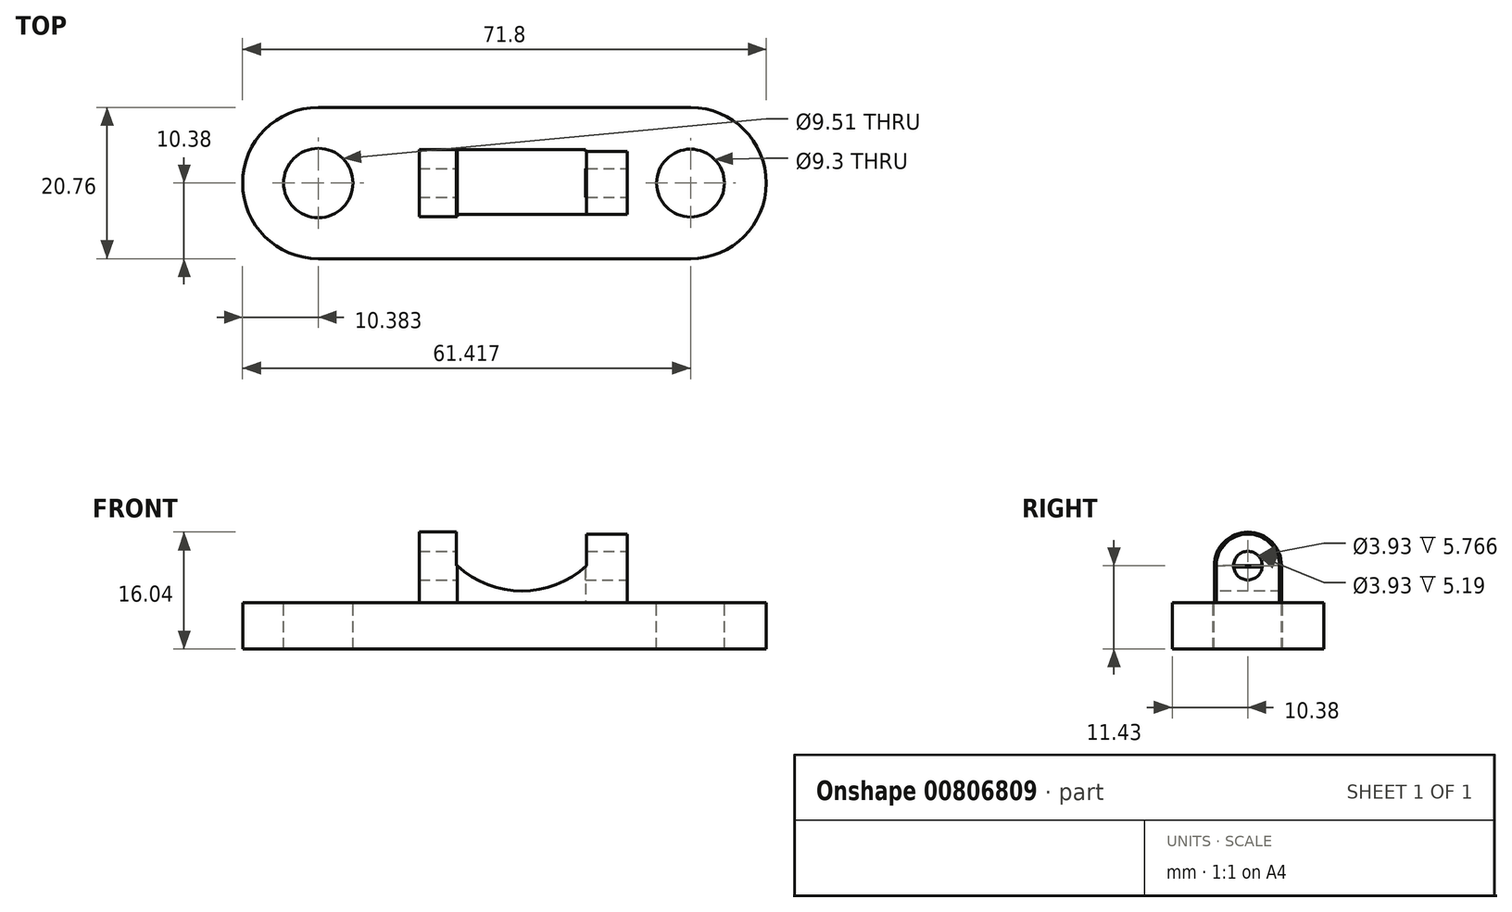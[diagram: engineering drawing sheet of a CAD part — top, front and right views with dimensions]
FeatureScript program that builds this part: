
annotation { "Feature Type Name" : "Feature", "Feature Type Description" : "" }
export const myFeature = defineFeature(function(context is Context, id is Id, definition is map)
    precondition{}
    {
        {
            var Q0;
            Q0=qCreatedBy(makeId("Top.planeOp"),FACE);
            var sketch = newSketch(context, id + "F0", { "sketchPlane" : qUnion([Q0])});
            skLineSegment(sketch, "E0.bottom", {"start": v(25.52, -10.38) * mm, "end": v(-25.52, -10.38) * mm});
            skLineSegment(sketch, "E0.top", {"start": v(25.52, 10.38) * mm, "end": v(-25.52, 10.38) * mm});
            skLineSegment(sketch, "E0.left", {"start": v(25.52, -10.38) * mm, "end": v(25.52, 10.38) * mm});
            skLineSegment(sketch, "E0.right", {"start": v(-25.52, -10.38) * mm, "end": v(-25.52, 10.38) * mm});
            skPoint(sketch, "E0.middle", {"position": v(0, 0) * mm});
            skArc(sketch, "E1", {"start": v(-25.52, 10.38) * mm, "mid": v(-35.9, 0) * mm, "end": v(-25.52, -10.38) * mm});
            skArc(sketch, "E2", {"start": v(25.52, -10.38) * mm, "mid": v(35.9, 0) * mm, "end": v(25.52, 10.38) * mm});
            skSolve(sketch);
        }
        {
            var Q0;
            Q0=makeQuery(id+"F0.imprint","IMPRINT",FACE,{"disambiguationData":[TD([[makeQuery(id+"F0.imprint","IMPRINT",EDGE,{"derivedFrom":sQuery(id+"F0.wireOp",EDGE,"E0.right")}),1.0]])]});
            var Q1;
            Q1=makeQuery(id+"F0.imprint","IMPRINT",FACE,{"disambiguationData":[TD([[makeQuery(id+"F0.imprint","IMPRINT",EDGE,{"derivedFrom":sQuery(id+"F0.wireOp",EDGE,"E0.bottom")}),-1.0]])]});
            var Q2;
            Q2=makeQuery(id+"F0.imprint","IMPRINT",FACE,{"disambiguationData":[TD([[makeQuery(id+"F0.imprint","IMPRINT",EDGE,{"derivedFrom":sQuery(id+"F0.wireOp",EDGE,"E0.left")}),-1.0]])]});
            extrude(context, id + "F1", {"entities" : qUnion([Q0, Q1, Q2]), "depth" : 25.4 * mm, "offsetDistance" : 25.4 * mm});
        }
        {
            var Q0;
            Q0=makeQuery(id+"F1.opExtrude","CAP_FACE",FACE,{"disambiguationData":[OSD([sQuery(id+"F0.wireOp",EDGE,"E0.bottom"),sQuery(id+"F0.wireOp",EDGE,"E0.top"),sQuery(id+"F0.wireOp",EDGE,"E1"),sQuery(id+"F0.wireOp",EDGE,"E2")])],"isStart":false});
            var sketch = newSketch(context, id + "F2", { "sketchPlane" : qUnion([Q0])});
            skCircle(sketch, "E3", {"center": v(-25.52, 0) * mm, "radius": 4.76 * mm});
            skCircle(sketch, "E4", {"center": v(25.52, 0) * mm, "radius": 4.65 * mm});
            skSolve(sketch);
        }
        {
            var Q0;
            Q0=makeQuery(id+"F2.imprint","IMPRINT",FACE,{"disambiguationData":[TD([[makeQuery(id+"F2.imprint","IMPRINT",EDGE,{"derivedFrom":sQuery(id+"F2.wireOp",EDGE,"E4")}),1.0]])]});
            var Q1;
            Q1=makeQuery(id+"F2.imprint","IMPRINT",FACE,{"disambiguationData":[TD([[makeQuery(id+"F2.imprint","IMPRINT",EDGE,{"derivedFrom":sQuery(id+"F2.wireOp",EDGE,"E3")}),1.0]])]});
            extrude(context, id + "F3", {"entities" : qUnion([Q0, Q1]), "operationType" : NewBodyOperationType.REMOVE, "oppositeDirection" : true, "depth" : 50.8 * mm, "offsetDistance" : 25.4 * mm});
        }
        {
            var Q0;
            Q0=makeQuery(id+"F1.opExtrude","CAP_FACE",FACE,{"disambiguationData":[OSD([sQuery(id+"F0.wireOp",EDGE,"E0.bottom"),sQuery(id+"F0.wireOp",EDGE,"E0.top"),sQuery(id+"F0.wireOp",EDGE,"E1"),sQuery(id+"F0.wireOp",EDGE,"E2")])],"isStart":false});
            extrude(context, id + "F4", {"entities" : qUnion([Q0]), "operationType" : NewBodyOperationType.REMOVE, "oppositeDirection" : true, "depth" : 19.05 * mm, "offsetDistance" : 25.4 * mm});
        }
        {
            var Q0;
            Q0=makeQuery(id+"F4.boolean.opBoolean","COPY",FACE,{"derivedFrom":makeQuery(id+"F4.opExtrude","CAP_FACE",FACE,{"disambiguationData":[OSD([sQuery(id+"F0.wireOp",EDGE,"E0.bottom"),sQuery(id+"F0.wireOp",EDGE,"E0.top"),sQuery(id+"F0.wireOp",EDGE,"E1"),sQuery(id+"F0.wireOp",EDGE,"E2")])],"isStart":false})});
            var sketch = newSketch(context, id + "F5", { "sketchPlane" : qUnion([Q0])});
            skLineSegment(sketch, "E5.bottom", {"start": v(-6.49, -4.61) * mm, "end": v(-11.68, -4.61) * mm});
            skLineSegment(sketch, "E5.top", {"start": v(-6.49, 4.61) * mm, "end": v(-11.68, 4.61) * mm});
            skLineSegment(sketch, "E5.left", {"start": v(-6.49, -4.61) * mm, "end": v(-6.49, 4.61) * mm});
            skLineSegment(sketch, "E5.right", {"start": v(-11.68, -4.61) * mm, "end": v(-11.68, 4.61) * mm});
            skPoint(sketch, "E5.middle", {"position": v(-9.08, 0) * mm});
            skLineSegment(sketch, "E6.bottom", {"start": v(16.87, -4.32) * mm, "end": v(11.1, -4.32) * mm});
            skLineSegment(sketch, "E6.top", {"start": v(16.87, 4.32) * mm, "end": v(11.1, 4.32) * mm});
            skLineSegment(sketch, "E6.left", {"start": v(16.87, -4.32) * mm, "end": v(16.87, 4.32) * mm});
            skLineSegment(sketch, "E6.right", {"start": v(11.1, -4.32) * mm, "end": v(11.1, 4.32) * mm});
            skPoint(sketch, "E6.middle", {"position": v(13.98, 0) * mm});
            skSolve(sketch);
        }
        {
            var Q0;
            Q0=makeQuery(id+"F5.imprint","IMPRINT",FACE,{"disambiguationData":[TD([[makeQuery(id+"F5.imprint","IMPRINT",EDGE,{"derivedFrom":sQuery(id+"F5.wireOp",EDGE,"E5.bottom")}),-1.0]])]});
            var Q1;
            Q1=makeQuery(id+"F5.imprint","IMPRINT",FACE,{"disambiguationData":[TD([[makeQuery(id+"F5.imprint","IMPRINT",EDGE,{"derivedFrom":sQuery(id+"F5.wireOp",EDGE,"E6.bottom")}),-1.0]])]});
            extrude(context, id + "F6", {"entities" : qUnion([Q0, Q1]), "operationType" : NewBodyOperationType.ADD, "depth" : 5.08 * mm, "offsetDistance" : 25.4 * mm});
        }
        {
            var Q0;
            Q0=makeQuery(id+"F6.opExtrude","SWEPT_FACE",FACE,{"disambiguationData":[OSD([sQuery(id+"F5.wireOp",EDGE,"E5.right")])]});
            var sketch = newSketch(context, id + "F7", { "sketchPlane" : qUnion([Q0])});
            skArc(sketch, "E7", {"start": v(4.61, 11.43) * mm, "mid": v(0, 16.04) * mm, "end": v(-4.61, 11.43) * mm});
            skSolve(sketch);
        }
        {
            var Q0;
            Q0=makeQuery(id+"F7.imprint","IMPRINT",FACE,{"disambiguationData":[TD([[makeQuery(id+"F7.imprint","IMPRINT",EDGE,{"derivedFrom":sQuery(id+"F7.wireOp",EDGE,"E7")}),1.0]])]});
            extrude(context, id + "F8", {"entities" : qUnion([Q0]), "operationType" : NewBodyOperationType.ADD, "depth" : -5.08 * mm, "offsetDistance" : 25.4 * mm});
        }
        {
            var Q0;
            Q0=makeQuery(id+"F6.opExtrude","SWEPT_FACE",FACE,{"disambiguationData":[OSD([sQuery(id+"F5.wireOp",EDGE,"E6.left")])]});
            var sketch = newSketch(context, id + "F9", { "sketchPlane" : qUnion([Q0])});
            skArc(sketch, "E8", {"start": v(4.32, 11.43) * mm, "mid": v(0, 15.75) * mm, "end": v(-4.32, 11.43) * mm});
            skSolve(sketch);
        }
        {
            var Q0;
            Q0=makeQuery(id+"F9.imprint","IMPRINT",FACE,{"disambiguationData":[TD([[makeQuery(id+"F9.imprint","IMPRINT",EDGE,{"derivedFrom":sQuery(id+"F9.wireOp",EDGE,"E8")}),1.0]])]});
            extrude(context, id + "F10", {"entities" : qUnion([Q0]), "operationType" : NewBodyOperationType.ADD, "depth" : -5.6 * mm, "offsetDistance" : 25.4 * mm});
        }
        {
            var Q0;
            {var subQ0=sQuery(id+"F5.wireOp",EDGE,"E6.left");Q0=makeQuery(id+"F10.boolean.opBoolean","MERGE",FACE,{"derivedFrom":[makeQuery(id+"F6.opExtrude","SWEPT_FACE",FACE,{"disambiguationData":[OSD([subQ0])]}),makeQuery(id+"F10.opExtrude","CAP_FACE",FACE,{"disambiguationData":[OSD([subQ0,sQuery(id+"F9.wireOp",EDGE,"E8")])],"isStart":true})]});}
            var sketch = newSketch(context, id + "F11", { "sketchPlane" : qUnion([Q0])});
            skCircle(sketch, "E9", {"center": v(0, 11.43) * mm, "radius": 1.96 * mm});
            skCircle(sketch, "E10", {"center": v(0, 11.43) * mm, "radius": 2.02 * mm});
            skSolve(sketch);
        }
        {
            var Q0;
            Q0=makeQuery(id+"F11.imprint","IMPRINT",FACE,{"disambiguationData":[TD([[makeQuery(id+"F11.imprint","IMPRINT",EDGE,{"derivedFrom":sQuery(id+"F11.wireOp",EDGE,"E9")}),1.0]])]});
            extrude(context, id + "F12", {"entities" : qUnion([Q0]), "operationType" : NewBodyOperationType.REMOVE, "oppositeDirection" : true, "depth" : 50.8 * mm, "offsetDistance" : 25.4 * mm});
        }
        {
            var Q0;
            Q0=makeQuery(id+"F4.boolean.opBoolean","COPY",FACE,{"derivedFrom":makeQuery(id+"F4.opExtrude","CAP_FACE",FACE,{"disambiguationData":[OSD([sQuery(id+"F0.wireOp",EDGE,"E0.bottom"),sQuery(id+"F0.wireOp",EDGE,"E0.top"),sQuery(id+"F0.wireOp",EDGE,"E1"),sQuery(id+"F0.wireOp",EDGE,"E2")])],"isStart":false})});
            var sketch = newSketch(context, id + "F13", { "sketchPlane" : qUnion([Q0])});
            skLineSegment(sketch, "E11.bottom", {"start": v(-6.49, 4.61) * mm, "end": v(11.1, 4.61) * mm});
            skLineSegment(sketch, "E11.top", {"start": v(-6.49, -4.32) * mm, "end": v(11.1, -4.32) * mm});
            skLineSegment(sketch, "E11.left", {"start": v(-6.49, 4.61) * mm, "end": v(-6.49, -4.32) * mm});
            skLineSegment(sketch, "E11.right", {"start": v(11.1, 4.61) * mm, "end": v(11.1, -4.32) * mm});
            skSolve(sketch);
        }
        {
            var Q0;
            {var subQ2=sQuery(id+"F13.wireOp",EDGE,"E11.bottom");Q0=makeQuery(id+"F13.imprint","IMPRINT",FACE,{"disambiguationData":[TD([[makeQuery(id+"F13.imprint","IMPRINT",EDGE,{"derivedFrom":subQ2}),-1.0]])]});}
            extrude(context, id + "F14", {"entities" : qUnion([Q0]), "operationType" : NewBodyOperationType.ADD, "depth" : 5.08 * mm, "offsetDistance" : 25.4 * mm});
        }
        {
            var Q0;
            Q0=makeQuery(id+"F14.boolean.opBoolean","MERGE",FACE,{"derivedFrom":[makeQuery(id+"F6.opExtrude","SWEPT_FACE",FACE,{"disambiguationData":[OSD([sQuery(id+"F5.wireOp",EDGE,"E6.bottom")])]}),makeQuery(id+"F14.opExtrude","SWEPT_FACE",FACE,{"disambiguationData":[OSD([sQuery(id+"F13.wireOp",EDGE,"E11.top")])]})]});
            var sketch = newSketch(context, id + "F15", { "sketchPlane" : qUnion([Q0])});
            skArc(sketch, "E12", {"start": v(-6.49, 11.43) * mm, "mid": v(2.4, 7.96) * mm, "end": v(11.28, 11.43) * mm});
            skSolve(sketch);
        }
        {
            var Q0;
            Q0=makeQuery(id+"F15.imprint","IMPRINT",FACE,{"disambiguationData":[TD([[makeQuery(id+"F15.imprint","IMPRINT",EDGE,{"derivedFrom":sQuery(id+"F15.wireOp",EDGE,"E12")}),1.0]])]});
            extrude(context, id + "F16", {"entities" : qUnion([Q0]), "operationType" : NewBodyOperationType.REMOVE, "oppositeDirection" : true, "depth" : 50.8 * mm, "offsetDistance" : 25.4 * mm});
        }
    });
